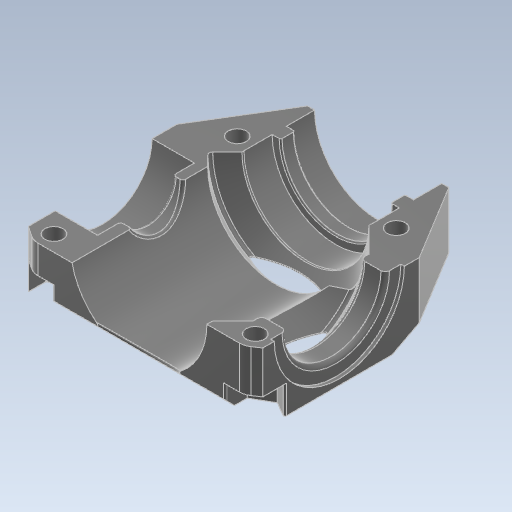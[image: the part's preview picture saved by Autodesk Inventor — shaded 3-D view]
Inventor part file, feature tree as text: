
AUTODESK INVENTOR PART (.ipt)
format: ipt  version: 2024 (Build 280153000, 153)  size: 505,344 bytes
history: native  units: mm
features: other x4, extrude x1, chamfer x1, fillet x1, sketch x1
ambient origin geometry x8: Origin, YZ Plane, XZ Plane, XY Plane, X Axis, Y Axis, Z Axis, Center Point
bodies: Body1 (feature_tree)
feature tree (8):
  other  "_bridseye_sketch.ipt"
  extrude  "押し出し2"  Depth=10.0mm
  chamfer  "面取り2"  Distance=0.2mm
  fillet  "フィレット1"  Radius=0.1mm
  other  "ソリッド16::_bridseye_sketch.ipt"
  other  "TaggingFeature1"
  other  "top_elbowUnit"
  sketch  "スケッチ3"
